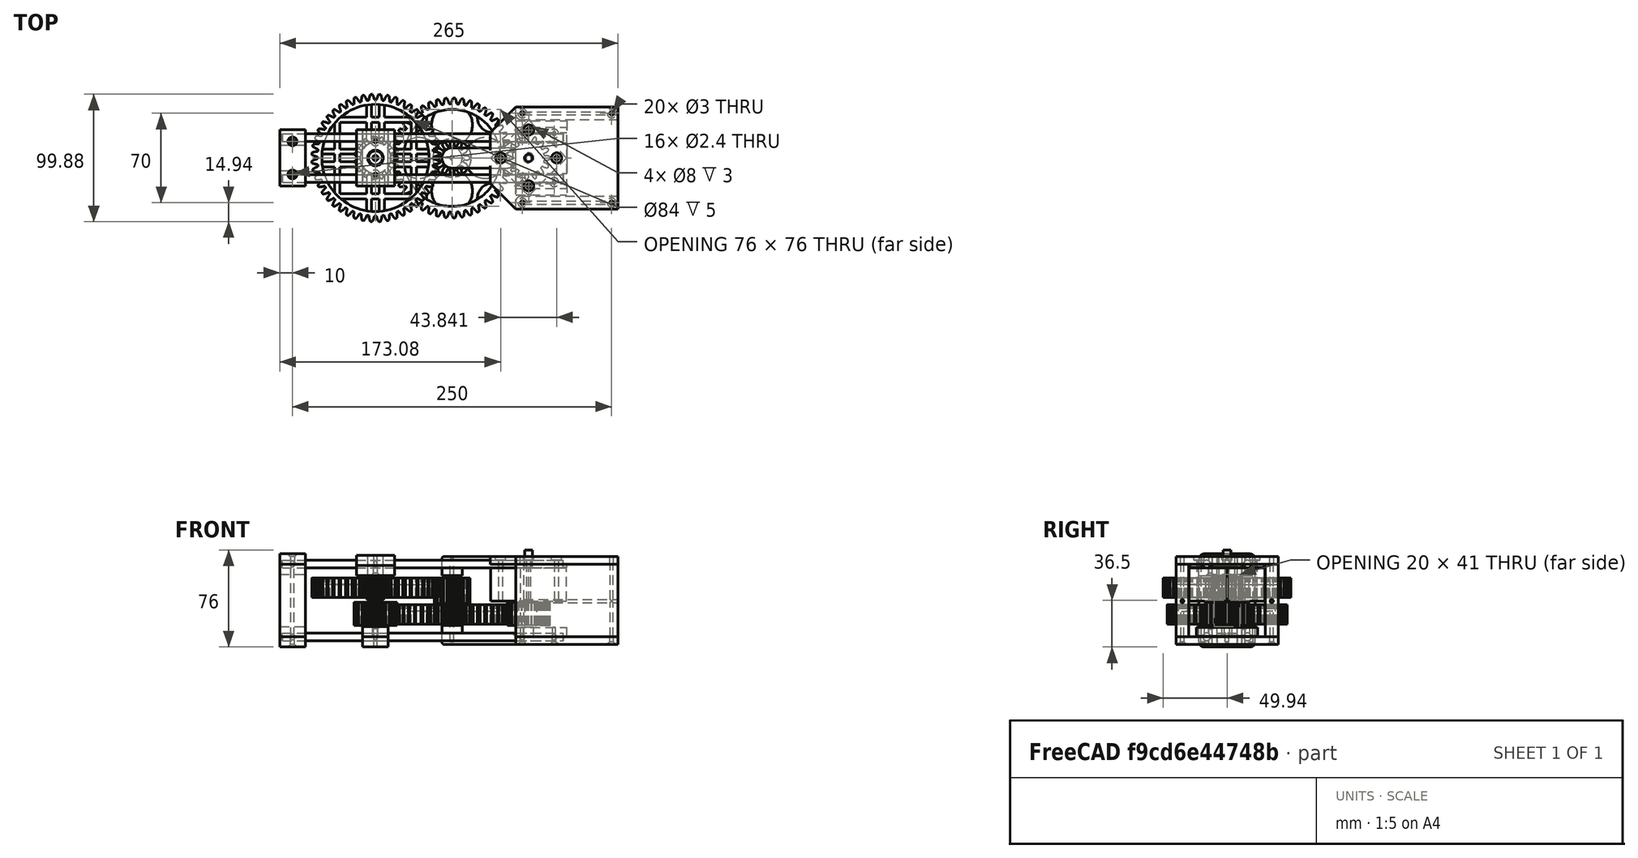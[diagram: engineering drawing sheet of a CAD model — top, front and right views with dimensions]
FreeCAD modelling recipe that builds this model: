
FCSTD DOCUMENT  (FreeCAD 0.18R16146 (Git))
Label: DoubleAxis2
License: All rights reserved
LicenseURL: http://en.wikipedia.org/wiki/All_rights_reserved
objects: Part::Cylinder×72, Part::MultiFuse×35, Part::Cut×28, Part::Box×21, Part::Feature×20, Part::Fillet×11, Part::Chamfer×6, Part::FeaturePython×5
note: 198 computed .brp shape members not serialized (recipe doc carries the construction recipe); baked Part::Feature solids carry a one-line shape summary decoded from their .brp

FEATURE [Part::Cylinder] Cylinder  label="CenterAxis"
  Angle = 360
  AttacherType = Attacher::AttachEngine3D
  Height = 100
  Placement = pos=(0,0,-10) rot=(0,0,1;0rad)
  Radius = 2.1
FEATURE [Part::FeaturePython] involutegear  label="MinuteGear"  # WARN: FeaturePython — macro-defined, semantics opaque (R4)
  Placement = pos=(0,0,1) rot=(0,0,1;0rad)
  backlash = 0
  beta = 0
  clearance = 0.25
  double_helix = false
  dw = 30
  head = 0
  height = 18
  module = 2
  numpoints = 6
  pressure_angle = 20
  properties_from_tool = false
  reversed_backlash = false
  shift = 0
  simple = false
  teeth = 15
  transverse_pitch = 6.28319
  undercut = false
  version = 0.0.3
FEATURE [Part::Cylinder] Cylinder004  label="Axis001"
  Angle = 360
  AttacherType = Attacher::AttachEngine3D
  Height = 50
  Radius = 2
FEATURE [Part::Cylinder] Cylinder005
  Angle = 360
  AttacherType = Attacher::AttachEngine3D
  Height = 19
  Placement = pos=(0,0,1) rot=(0,0,1;0rad)
  Radius = 6.5
FEATURE [Part::MultiFuse] Fusion
  Shapes = -> [Cylinder005,involutegear]
FEATURE [Part::Cut] Cut002  label="MinuteHandGear"
  Base = -> Fusion
  Placement = pos=(-60,0,0) rot=(0,0,1;0rad)
  Tool = -> Cylinder004
FEATURE [Part::Cylinder] Cylinder006  label="Bearing003"
  Angle = 360
  AttacherType = Attacher::AttachEngine3D
  Height = 15
  Placement = pos=(0,0,21) rot=(0,0,1;0rad)
  Radius = 5.5
FEATURE [Part::Cylinder] Cylinder007  label="Bearing002"
  Angle = 360
  AttacherType = Attacher::AttachEngine3D
  Height = 2
  Placement = pos=(0,0,21) rot=(0,0,1;0rad)
  Radius = 6.5
FEATURE [Part::MultiFuse] Fusion001  label="CenterBearingBody"
  Shapes = -> [Cylinder007,Cylinder006]
FEATURE [Part::Feature] Fusion001002004  label="Cutout005"
  Placement = pos=(0,0,0) rot=(0,0,-1;1.5708rad)
  shape: bbox 35 x 44.41 x 10 mm, 12 faces, 2 solids (baked)
FEATURE [Part::FeaturePython] involutegear002  label="HourGear"  # WARN: FeaturePython — macro-defined, semantics opaque (R4)
  Placement = pos=(0,0,0) rot=(0,0,1;0.064577rad)
  backlash = 0
  beta = 0
  clearance = 0.25
  double_helix = false
  dw = 96
  head = 0
  height = 15
  module = 2
  numpoints = 6
  pressure_angle = 20
  properties_from_tool = false
  reversed_backlash = false
  shift = 0
  simple = false
  teeth = 48
  transverse_pitch = 6.28319
  undercut = false
  version = 0.0.3
FEATURE [Part::Feature] Fusion001002003  label="Cutout004"
  Placement = pos=(0,0,0) rot=(0,0,1;3.14159rad)
  shape: bbox 44.41 x 35 x 10 mm, 12 faces, 2 solids (baked)
FEATURE [Part::Feature] Fusion001002002  label="Cutout003"
  Placement = pos=(0,0,0) rot=(0,0,1;1.5708rad)
  shape: bbox 35 x 44.41 x 10 mm, 12 faces, 2 solids (baked)
FEATURE [Part::Feature] Fusion001002001  label="Cutout002"
  shape: bbox 44.41 x 35 x 10 mm, 12 faces, 2 solids (baked)
FEATURE [Part::MultiFuse] Fusion001002005
  Shapes = -> [Fusion001002004,Fusion001002002,Fusion001002001,Fusion001002003]
FEATURE [Part::Cylinder] Cylinder008  label="Axis002"
  Angle = 360
  AttacherType = Attacher::AttachEngine3D
  Height = 16
  Radius = 12
FEATURE [Part::Cylinder] Cylinder009  label="Cutout001"
  Angle = 360
  AttacherType = Attacher::AttachEngine3D
  Height = 10
  Placement = pos=(0,0,10) rot=(0,0,1;0rad)
  Radius = 42
FEATURE [Part::Box] Box002  label="Cube002"
  AttacherType = Attacher::AttachEngine3D
  Height = 10
  Length = 64
  Placement = pos=(-32,-32,0) rot=(0,0,1;0rad)
  Width = 64
FEATURE [Part::Box] Box003  label="Cube003"
  AttacherType = Attacher::AttachEngine3D
  Height = 10
  Length = 56
  Placement = pos=(-28,-28,0) rot=(0,0,1;0rad)
  Width = 56
FEATURE [Part::Cut] Cut009
  Base = -> Box002
  Tool = -> Box003
FEATURE [Part::Cylinder] Cylinder012  label="Axis003"
  Angle = 360
  AttacherType = Attacher::AttachEngine3D
  Height = 50
  Radius = 6
FEATURE [Part::Cut] Cut
  Base = -> involutegear002
  Tool = -> Cylinder009
FEATURE [Part::MultiFuse] Fusion001002006
  Shapes = -> [Cut,Cylinder008]
FEATURE [Part::Cut] Cut010
  Base = -> Fusion001002006
  Tool = -> Fusion001002005
FEATURE [Part::MultiFuse] Fusion001002007
  Shapes = -> [Cut010,Cut009]
FEATURE [Part::Cut] Cut011  label="HourHandGear"
  Base = -> Fusion001002007
  Placement = pos=(-60,0,23) rot=(0,0,1;0rad)
  Tool = -> Cylinder012
FEATURE [Part::Cut] Cut012  label="CenterBearing001"
  Base = -> Fusion001
  Placement = pos=(-60,0,0) rot=(0,0,1;0rad)
  Tool = -> Cylinder
FEATURE [Part::FeaturePython] involutegear001  label="Couple001"  # WARN: FeaturePython — macro-defined, semantics opaque (R4)
  Placement = pos=(0,0,2) rot=(0,0,1;0rad)
  backlash = 0
  beta = 0
  clearance = 0.25
  double_helix = false
  dw = 90
  head = 0
  height = 15
  module = 2
  numpoints = 6
  pressure_angle = 20
  properties_from_tool = false
  reversed_backlash = false
  shift = 0
  simple = false
  teeth = 45
  transverse_pitch = 6.28319
  undercut = false
  version = 0.0.3
FEATURE [Part::FeaturePython] involutegear004  label="Couple003"  # WARN: FeaturePython — macro-defined, semantics opaque (R4)
  Placement = pos=(0,0,10) rot=(0,0,1;0rad)
  backlash = 0
  beta = 0
  clearance = 0.25
  double_helix = false
  dw = 24
  head = 0
  height = 28
  module = 2
  numpoints = 6
  pressure_angle = 20
  properties_from_tool = false
  reversed_backlash = false
  shift = 0
  simple = false
  teeth = 12
  transverse_pitch = 6.28319
  undercut = false
  version = 0.0.3
FEATURE [Part::FeaturePython] involutegear005  label="MotorGear002"  # WARN: FeaturePython — macro-defined, semantics opaque (R4)
  Placement = pos=(60,0,1) rot=(0,0,1;0rad)
  backlash = 0
  beta = 0
  clearance = 0.25
  double_helix = false
  dw = 30
  head = 0
  height = 18
  module = 2
  numpoints = 6
  pressure_angle = 20
  properties_from_tool = false
  reversed_backlash = false
  shift = 0
  simple = false
  teeth = 15
  transverse_pitch = 6.28319
  undercut = false
  version = 0.0.3
FEATURE [Part::Cylinder] Cylinder013  label="Cutout006"
  Angle = 360
  AttacherType = Attacher::AttachEngine3D
  Height = 5
  Placement = pos=(0,0,12) rot=(0,0,1;0rad)
  Radius = 38
FEATURE [Part::Cylinder] Cylinder014  label="Cylinder"
  Angle = 360
  AttacherType = Attacher::AttachEngine3D
  Height = 16
  Placement = pos=(0,0,2) rot=(0,0,1;0rad)
  Radius = 15
FEATURE [Part::Feature] Cut015001  label="Cut016"
  shape: bbox 28 x 48.41 x 16 mm, 8 faces, 2 solids (baked)
FEATURE [Part::Feature] Cut015002  label="Cut017"
  Placement = pos=(0,0,0) rot=(0,0,1;1.5708rad)
  shape: bbox 48.41 x 28 x 16 mm, 8 faces, 2 solids (baked)
FEATURE [Part::Feature] Cut015003  label="Cut018"
  Placement = pos=(0,0,0) rot=(0,0,1;3.14159rad)
  shape: bbox 28 x 48.41 x 16 mm, 8 faces, 2 solids (baked)
FEATURE [Part::Feature] Cut015004  label="Cut019"
  Placement = pos=(0,0,0) rot=(0,0,-1;1.5708rad)
  shape: bbox 48.41 x 28 x 16 mm, 8 faces, 2 solids (baked)
FEATURE [Part::MultiFuse] Fusion001002009
  Placement = pos=(0,0,-3) rot=(0,0,1;0rad)
  Shapes = -> [Cut015004,Cut015003,Cut015001,Cut015002]
FEATURE [Part::MultiFuse] Fusion001002010
  Shapes = -> [Cylinder013,Fusion001002009]
FEATURE [Part::Cut] Cut015005
  Base = -> involutegear001
  Tool = -> Fusion001002010
FEATURE [Part::Cylinder] Cylinder015  label="Cylinder006"
  Angle = 360
  AttacherType = Attacher::AttachEngine3D
  Height = 9
  Placement = pos=(0,0,30) rot=(0,0,1;0rad)
  Radius = 8
FEATURE [Part::MultiFuse] Fusion001002011
  Shapes = -> [Cylinder015,Cut015005,Cylinder014,involutegear004]
FEATURE [Part::Cylinder] Cylinder016  label="Axis004"
  Angle = 360
  AttacherType = Attacher::AttachEngine3D
  Height = 50
  Radius = 1.6
FEATURE [Part::Cut] Cut015006  label="CouplingGear001"
  Base = -> Fusion001002011
  Tool = -> Cylinder016
FEATURE [Part::Cylinder] Cylinder017  label="MotorAxis"
  Angle = 360
  AttacherType = Attacher::AttachEngine3D
  Height = 50
  Placement = pos=(60,0,0) rot=(0,0,1;0rad)
  Radius = 2
FEATURE [Part::Cut] Cut015007  label="MotorGear"
  Base = -> involutegear005
  Tool = -> Cylinder017
FEATURE [Part::Box] Box004  label="BottomBase001"
  AttacherType = Attacher::AttachEngine3D
  Height = 8
  Length = 20
  Placement = pos=(-135,-22,-16) rot=(0,0,1;0rad)
  Width = 44
FEATURE [Part::Cylinder] Cylinder020  label="ScrewHole"
  Angle = 360
  AttacherType = Attacher::AttachEngine3D
  Height = 40
  Placement = pos=(-125,13,-20) rot=(0,0,1;0rad)
  Radius = 1.5
FEATURE [Part::Cylinder] Cylinder021  label="ScrewHole001"
  Angle = 360
  AttacherType = Attacher::AttachEngine3D
  Height = 40
  Placement = pos=(-125,-13,-20) rot=(0,0,1;0rad)
  Radius = 1.5
FEATURE [Part::Box] Box005  label="BottomBase002"
  AttacherType = Attacher::AttachEngine3D
  Height = 57
  Length = 20
  Placement = pos=(-135,-22,-8) rot=(0,0,1;0rad)
  Width = 44
FEATURE [Part::Cylinder] Cylinder025  label="ScrewHole005"
  Angle = 360
  AttacherType = Attacher::AttachEngine3D
  Height = 100
  Placement = pos=(-125,-13,-20) rot=(0,0,1;0rad)
  Radius = 1.2
FEATURE [Part::Cylinder] Cylinder026  label="ScrewHole006"
  Angle = 360
  AttacherType = Attacher::AttachEngine3D
  Height = 100
  Placement = pos=(-125,13,-20) rot=(0,0,1;0rad)
  Radius = 1.2
FEATURE [Part::MultiFuse] Fusion001002012004
  Shapes = -> [Cylinder026,Cylinder025]
FEATURE [Part::Fillet] Fillet
  Base = -> Box004
  Edges = 2 edges r=4: [Edge9,Edge11]
FEATURE [Part::Box] Box008  label="BottomBase005"
  AttacherType = Attacher::AttachEngine3D
  Height = 41
  Length = 20
  Placement = pos=(-135,-10,0) rot=(0,0,1;0rad)
  Width = 20
FEATURE [Part::Fillet] Fillet002
  Base = -> Box008
  Edges = 4 edges r=9: [Edge9,Edge10,Edge11,Edge12]
FEATURE [Part::Box] Box009  label="MotorBody"
  AttacherType = Attacher::AttachEngine3D
  Height = 26
  Length = 42
  Placement = pos=(-21,-21,20) rot=(0,0,1;0rad)
  Width = 42
FEATURE [Part::Cylinder] Cylinder032  label="ScrewHole011"
  Angle = 360
  AttacherType = Attacher::AttachEngine3D
  Height = 50
  Placement = pos=(15.5,15.5,0) rot=(0,0,1;0rad)
  Radius = 1.6
FEATURE [Part::Cylinder] Cylinder033  label="ScrewHole002"
  Angle = 360
  AttacherType = Attacher::AttachEngine3D
  Height = 50
  Placement = pos=(-15.5,15.5,0) rot=(0,0,1;0rad)
  Radius = 1.6
FEATURE [Part::Cylinder] Cylinder034  label="ScrewHole012"
  Angle = 360
  AttacherType = Attacher::AttachEngine3D
  Height = 50
  Placement = pos=(15.5,-15.5,0) rot=(0,0,1;0rad)
  Radius = 1.6
FEATURE [Part::Cylinder] Cylinder035  label="ScrewHole013"
  Angle = 360
  AttacherType = Attacher::AttachEngine3D
  Height = 50
  Placement = pos=(-15.5,-15.5,0) rot=(0,0,1;0rad)
  Radius = 1.6
FEATURE [Part::MultiFuse] Fusion001002012013  label="MotorScrewHoles"
  Shapes = -> [Cylinder035,Cylinder033,Cylinder034,Cylinder032]
FEATURE [Part::Cut] Cut015008  label="MotorBody001"
  Base = -> Box009
  Tool = -> Fusion001002012013
FEATURE [Part::Cylinder] Cylinder036  label="MotorAxis001"
  Angle = 360
  AttacherType = Attacher::AttachEngine3D
  Height = 20
  Placement = pos=(0,0,40) rot=(0,0,1;0rad)
  Radius = 3
FEATURE [Part::MultiFuse] Fusion001002014  label="MotorModel"
  Placement = pos=(60,0,0) rot=(0,0,1;0.785398rad)
  Shapes = -> [Cut015008,Cylinder036]
FEATURE [Part::Cylinder] Cylinder037  label="HourAxis"
  Angle = 360
  AttacherType = Attacher::AttachEngine3D
  Height = 50
  Placement = pos=(-60,0,30) rot=(0,0,1;0rad)
  Radius = 6.1
FEATURE [Part::Box] Box019  label="BottomBase015"
  AttacherType = Attacher::AttachEngine3D
  Height = 8
  Length = 30
  Placement = pos=(-75,-22,40) rot=(0,0,1;0rad)
  Width = 44
FEATURE [Part::Cut] Cut015017007002
  Base = -> Box019
  Tool = -> Cylinder037
FEATURE [Part::Cylinder] Cylinder038  label="ScrewHole014"
  Angle = 360
  AttacherType = Attacher::AttachEngine3D
  Height = 100
  Placement = pos=(-60,-13,-20) rot=(0,0,1;0rad)
  Radius = 1.5
FEATURE [Part::Cylinder] Cylinder039  label="ScrewHole015"
  Angle = 360
  AttacherType = Attacher::AttachEngine3D
  Height = 100
  Placement = pos=(-60,13,-20) rot=(0,0,1;0rad)
  Radius = 1.5
FEATURE [Part::MultiFuse] Fusion001002012021
  Shapes = -> [Cylinder039,Cylinder038]
FEATURE [Part::Cut] Cut015017007003  label="HandCap001Body"
  Base = -> Cut015017007002
  Tool = -> Fusion001002012021
FEATURE [Part::Chamfer] Chamfer002  label="HandCap001"
  Base = -> Cut015017007003
  Edges = 2 edges r=2: [Edge16,Edge18]
FEATURE [Part::Box] Box  label="BoxBase"
  AttacherType = Attacher::AttachEngine3D
  Height = 6
  Length = 100
  Placement = pos=(30,-40,49) rot=(0,0,1;0rad)
  Width = 80
FEATURE [Part::Box] Box021  label="BoxBase001"
  AttacherType = Attacher::AttachEngine3D
  Height = 8.5
  Length = 90
  Placement = pos=(0,-8,46.5) rot=(0,0,1;0rad)
  Width = 16
FEATURE [Part::Cylinder] Cylinder043  label="Cylinder007"
  Angle = 360
  AttacherType = Attacher::AttachEngine3D
  Height = 15
  Placement = pos=(0,0,40) rot=(0,0,1;0rad)
  Radius = 8
FEATURE [Part::Fillet] Fillet010
  Base = -> Cylinder043
  Edges = 1 edges r=2: [Edge1]
FEATURE [Part::Cylinder] Cylinder047  label="Column003"
  Angle = 360
  AttacherType = Attacher::AttachEngine3D
  Height = 220
  Placement = pos=(-133,-16,-8) rot=(0,1,0;1.5708rad)
  Radius = 3
FEATURE [Part::Cylinder] Cylinder048  label="Column004"
  Angle = 360
  AttacherType = Attacher::AttachEngine3D
  Height = 220
  Placement = pos=(-133,16,-8) rot=(0,1,0;1.5708rad)
  Radius = 3
FEATURE [Part::MultiFuse] Fusion001002012029  label="BottomPilars"
  Shapes = -> [Cylinder047,Cylinder048]
FEATURE [Part::Cylinder] Cylinder049  label="Column005"
  Angle = 360
  AttacherType = Attacher::AttachEngine3D
  Height = 220
  Placement = pos=(-133,-16,49) rot=(0,1,0;1.5708rad)
  Radius = 3
FEATURE [Part::Cylinder] Cylinder050  label="Column006"
  Angle = 360
  AttacherType = Attacher::AttachEngine3D
  Height = 220
  Placement = pos=(-133,16,49) rot=(0,1,0;1.5708rad)
  Radius = 3
FEATURE [Part::MultiFuse] Fusion001002012030  label="TopPilars001"
  Shapes = -> [Cylinder049,Cylinder050]
FEATURE [Part::Feature] Fusion001002012029001  label="BottomPilars001"
  shape: bbox 220 x 38 x 6 mm, 6 faces, 2 solids (baked)
FEATURE [Part::MultiFuse] Fusion001002012029002
  Shapes = -> [Cylinder020,Cylinder021,Fusion001002012029001]
FEATURE [Part::Cut] Cut015017007008
  Base = -> Fillet
  Tool = -> Fusion001002012029002
FEATURE [Part::Chamfer] Chamfer  label="Cap001"
  Base = -> Cut015017007008
  Edges = 2 edges r=2: [Edge28,Edge29]
FEATURE [Part::Feature] Fusion001002012029003  label="BottomPilars002"
  shape: bbox 220 x 38 x 6 mm, 6 faces, 2 solids (baked)
FEATURE [Part::Feature] Fusion001002012030001  label="TopPilars002"
  shape: bbox 220 x 38 x 6 mm, 6 faces, 2 solids (baked)
FEATURE [Part::MultiFuse] Fusion001002012030002
  Shapes = -> [Fusion001002012004,Fillet002,Fusion001002012029003,Fusion001002012030001]
FEATURE [Part::Cut] Cut015017007009  label="CapJoin001"
  Base = -> Box005
  Tool = -> Fusion001002012030002
FEATURE [Part::Feature] Chamfer003  label="Cap002"
  Placement = pos=(0,0,41) rot=(1,0,0;3.14159rad)
  shape: bbox 20 x 44 x 8 mm, 16 faces (baked)
FEATURE [Part::Box] Box022  label="BottomBase017"
  AttacherType = Attacher::AttachEngine3D
  Height = 8
  Length = 20
  Placement = pos=(-70,-22,-8) rot=(0,0,1;0rad)
  Width = 44
FEATURE [Part::Cylinder] Cylinder051  label="ScrewHole018"
  Angle = 360
  AttacherType = Attacher::AttachEngine3D
  Height = 100
  Placement = pos=(-125,-13,-20) rot=(0,0,1;0rad)
  Radius = 1.5
FEATURE [Part::Cylinder] Cylinder052  label="ScrewHole019"
  Angle = 360
  AttacherType = Attacher::AttachEngine3D
  Height = 100
  Placement = pos=(-125,13,-20) rot=(0,0,1;0rad)
  Radius = 1.5
FEATURE [Part::MultiFuse] Fusion001002012030003
  Placement = pos=(65,0,0) rot=(0,0,1;0rad)
  Shapes = -> [Cylinder052,Cylinder051]
FEATURE [Part::Cylinder] Cylinder053  label="MinuteHandAxis"
  Angle = 360
  AttacherType = Attacher::AttachEngine3D
  Height = 60
  Placement = pos=(-60,0,-20) rot=(0,0,1;0rad)
  Radius = 2.1
FEATURE [Part::MultiFuse] Fusion001002012030004
  Shapes = -> [Fusion001002012030003,Cylinder053]
FEATURE [Part::Cut] Cut015017007010  label="Cap004Body"
  Base = -> Box022
  Tool = -> Fusion001002012030004
FEATURE [Part::Feature] Fusion001002012030005  label="TopPilars003"
  shape: bbox 220 x 38 x 6 mm, 6 faces, 2 solids (baked)
FEATURE [Part::Cut] Cut015017007011  label="Cap005"
  Base = -> Chamfer002
  Tool = -> Fusion001002012030005
FEATURE [Part::Box] Box023  label="BottomBase018"
  AttacherType = Attacher::AttachEngine3D
  Height = 8
  Length = 30
  Placement = pos=(-75,-22,48) rot=(0,0,1;0rad)
  Width = 44
FEATURE [Part::Cylinder] Cylinder054  label="ScrewHole020"
  Angle = 360
  AttacherType = Attacher::AttachEngine3D
  Height = 100
  Placement = pos=(-125,-13,-20) rot=(0,0,1;0rad)
  Radius = 1.2
FEATURE [Part::Cylinder] Cylinder055  label="ScrewHole021"
  Angle = 360
  AttacherType = Attacher::AttachEngine3D
  Height = 100
  Placement = pos=(-125,13,-20) rot=(0,0,1;0rad)
  Radius = 1.2
FEATURE [Part::MultiFuse] Fusion001002012030006
  Placement = pos=(65,0,0) rot=(0,0,1;0rad)
  Shapes = -> [Cylinder055,Cylinder054]
FEATURE [Part::Cylinder] Cylinder056  label="HourHandAxis001"
  Angle = 360
  AttacherType = Attacher::AttachEngine3D
  Height = 60
  Placement = pos=(-60,0,30) rot=(0,0,1;0rad)
  Radius = 6.1
FEATURE [Part::MultiFuse] Fusion001002012030007
  Shapes = -> [Fusion001002012030006,Cylinder056]
FEATURE [Part::Fillet] Fillet011
  Base = -> Box023
  Edges = 2 edges r=4: [Edge10,Edge12]
FEATURE [Part::Cut] Cut015017007012
  Base = -> Fillet011
  Tool = -> Fusion001002012030007
FEATURE [Part::Feature] Fusion001002012030008  label="TopPilars004"
  shape: bbox 220 x 38 x 6 mm, 6 faces, 2 solids (baked)
FEATURE [Part::Cut] Cut015017007013  label="Cap006"
  Base = -> Cut015017007012
  Tool = -> Fusion001002012030008
FEATURE [Part::Chamfer] Chamfer004  label="Cap004Body002"
  Base = -> Cut015017007010
  Edges = 2 edges r=2: [Edge10,Edge12]
FEATURE [Part::Box] Box024  label="BottomBase019"
  AttacherType = Attacher::AttachEngine3D
  Height = 8
  Length = 20
  Placement = pos=(-70,-22,-16) rot=(0,0,1;0rad)
  Width = 44
FEATURE [Part::Cylinder] Cylinder057  label="ScrewHole022"
  Angle = 360
  AttacherType = Attacher::AttachEngine3D
  Height = 100
  Placement = pos=(-125,-13,-20) rot=(0,0,1;0rad)
  Radius = 1.2
FEATURE [Part::Cylinder] Cylinder058  label="ScrewHole023"
  Angle = 360
  AttacherType = Attacher::AttachEngine3D
  Height = 100
  Placement = pos=(-125,13,-20) rot=(0,0,1;0rad)
  Radius = 1.2
FEATURE [Part::MultiFuse] Fusion001002012030009
  Placement = pos=(65,0,0) rot=(0,0,1;0rad)
  Shapes = -> [Cylinder058,Cylinder057]
FEATURE [Part::Fillet] Fillet012
  Base = -> Box024
  Edges = 2 edges r=4: [Edge9,Edge11]
FEATURE [Part::Feature] Fusion001002012029004  label="BottomPilars003"
  shape: bbox 220 x 38 x 6 mm, 6 faces, 2 solids (baked)
FEATURE [Part::Cut] Cut015017007014  label="Cap003Body"
  Base = -> Fillet012
  Tool = -> Fusion001002012029004
FEATURE [Part::Feature] Fusion001002012030010  label="BottomPilars004"
  shape: bbox 220 x 38 x 6 mm, 6 faces, 2 solids (baked)
FEATURE [Part::Cut] Cut015017007015  label="Cap004"
  Base = -> Chamfer004
  Tool = -> Fusion001002012030010
FEATURE [Part::Cut] Cut015017007016  label="Cap003"
  Base = -> Cut015017007014
  Tool = -> Fusion001002012030009
FEATURE [Part::Fillet] Fillet008
  Base = -> Box021
  Edges = 2 edges r=4: [Edge5,Edge7]
FEATURE [Part::Fillet] Fillet009
  Base = -> Fillet008
  Edges = 1 edges r=2: [Edge5]
FEATURE [Part::Box] Box025  label="BoxBase002"
  AttacherType = Attacher::AttachEngine3D
  Height = 8
  Length = 50
  Placement = pos=(40,-12,46.5) rot=(0,0,1;0rad)
  Width = 24
FEATURE [Part::Box] Box027  label="BoxBase004"
  AttacherType = Attacher::AttachEngine3D
  Height = 8
  Length = 40
  Placement = pos=(50,20,46.5) rot=(0,0,1;0rad)
  Width = 9
FEATURE [Part::Cylinder] Cylinder059  label="ScrewHole024"
  Angle = 360
  AttacherType = Attacher::AttachEngine3D
  Height = 50
  Placement = pos=(-15.5,15.5,0) rot=(0,0,1;0rad)
  Radius = 1.6
FEATURE [Part::Cylinder] Cylinder060  label="ScrewHole025"
  Angle = 360
  AttacherType = Attacher::AttachEngine3D
  Height = 50
  Placement = pos=(15.5,15.5,0) rot=(0,0,1;0rad)
  Radius = 1.6
FEATURE [Part::Cylinder] Cylinder061  label="ScrewHole026"
  Angle = 360
  AttacherType = Attacher::AttachEngine3D
  Height = 50
  Placement = pos=(15.5,-15.5,0) rot=(0,0,1;0rad)
  Radius = 1.6
FEATURE [Part::Cylinder] Cylinder062  label="ScrewHole027"
  Angle = 360
  AttacherType = Attacher::AttachEngine3D
  Height = 50
  Placement = pos=(-15.5,-15.5,0) rot=(0,0,1;0rad)
  Radius = 1.6
FEATURE [Part::MultiFuse] Fusion001002012030013  label="MotorScrewHoles001"
  Placement = pos=(60,0,20) rot=(0,0,1;0.785398rad)
  Shapes = -> [Cylinder062,Cylinder059,Cylinder061,Cylinder060]
FEATURE [Part::Cylinder] Cylinder063  label="ScrewHole028"
  Angle = 360
  AttacherType = Attacher::AttachEngine3D
  Height = 50
  Placement = pos=(15.5,-15.5,0) rot=(0,0,1;0rad)
  Radius = 4
FEATURE [Part::Cylinder] Cylinder064  label="ScrewHole029"
  Angle = 360
  AttacherType = Attacher::AttachEngine3D
  Height = 50
  Placement = pos=(15.5,15.5,0) rot=(0,0,1;0rad)
  Radius = 4
FEATURE [Part::Cylinder] Cylinder065  label="ScrewHole030"
  Angle = 360
  AttacherType = Attacher::AttachEngine3D
  Height = 50
  Placement = pos=(-15.5,15.5,0) rot=(0,0,1;0rad)
  Radius = 4
FEATURE [Part::Cylinder] Cylinder066  label="ScrewHole031"
  Angle = 360
  AttacherType = Attacher::AttachEngine3D
  Height = 50
  Placement = pos=(-15.5,-15.5,0) rot=(0,0,1;0rad)
  Radius = 4
FEATURE [Part::MultiFuse] Fusion001002012030014  label="MotorScrewHoles002"
  Placement = pos=(60,0,52) rot=(0,0,1;0.785398rad)
  Shapes = -> [Cylinder066,Cylinder065,Cylinder063,Cylinder064]
FEATURE [Part::Box] Box026  label="BoxBase003"
  AttacherType = Attacher::AttachEngine3D
  Height = 8
  Length = 40
  Placement = pos=(50,-29,46.5) rot=(0,0,1;0rad)
  Width = 9
FEATURE [Part::MultiFuse] Fusion001002012030011  label="BoxBase005"
  Shapes = -> [Fillet009,Box026,Box025,Box027,Box]
FEATURE [Part::MultiFuse] Fusion001002012030012  label="BoxBase006"
  Shapes = -> [Fusion001002012030011,Fillet010]
FEATURE [Part::Cylinder] Cylinder067  label="ScrewHole032"
  Angle = 360
  AttacherType = Attacher::AttachEngine3D
  Height = 50
  Placement = pos=(55,-35,0) rot=(0,0,1;0rad)
  Radius = 1.5
FEATURE [Part::Cylinder] Cylinder068  label="ScrewHole033"
  Angle = 360
  AttacherType = Attacher::AttachEngine3D
  Height = 50
  Placement = pos=(55,35,0) rot=(0,0,1;0rad)
  Radius = 1.5
FEATURE [Part::Cylinder] Cylinder069  label="ScrewHole034"
  Angle = 360
  AttacherType = Attacher::AttachEngine3D
  Height = 50
  Placement = pos=(125,35,0) rot=(0,0,1;0rad)
  Radius = 1.5
FEATURE [Part::Cylinder] Cylinder070  label="ScrewHole035"
  Angle = 360
  AttacherType = Attacher::AttachEngine3D
  Height = 50
  Placement = pos=(125,-35,0) rot=(0,0,1;0rad)
  Radius = 1.5
FEATURE [Part::MultiFuse] Fusion001002012030015  label="BoxScrewHoles"
  Placement = pos=(0,0,30) rot=(0,0,1;0rad)
  Shapes = -> [Cylinder070,Cylinder069,Cylinder067,Cylinder068]
FEATURE [Part::Cylinder] Cylinder071  label="ScrewHole036"
  Angle = 360
  AttacherType = Attacher::AttachEngine3D
  Height = 20
  Placement = pos=(0,0,33) rot=(0,0,1;0rad)
  Radius = 1.5
FEATURE [Part::MultiFuse] Fusion001002012030016  label="BoxHoles"
  Shapes = -> [Cylinder071,Fusion001002012030015,Fusion001002012030014,Fusion001002012030013]
FEATURE [Part::Feature] Fusion001002012030017  label="TopPilars005"
  shape: bbox 220 x 38 x 6 mm, 6 faces, 2 solids (baked)
FEATURE [Part::Box] Box030  label="BoxBase008"
  AttacherType = Attacher::AttachEngine3D
  Height = 8.5
  Length = 90
  Placement = pos=(0,-8,-14) rot=(0,0,1;0rad)
  Width = 16
FEATURE [Part::Cylinder] Cylinder077  label="Cylinder008"
  Angle = 360
  AttacherType = Attacher::AttachEngine3D
  Height = 15
  Placement = pos=(0,0,-14) rot=(0,0,1;0rad)
  Radius = 8
FEATURE [Part::Cylinder] Cylinder086  label="ScrewHole049"
  Angle = 360
  AttacherType = Attacher::AttachEngine3D
  Height = 50
  Placement = pos=(125,35,-20) rot=(0,0,1;0rad)
  Radius = 1.5
FEATURE [Part::Cylinder] Cylinder087  label="ScrewHole050"
  Angle = 360
  AttacherType = Attacher::AttachEngine3D
  Height = 50
  Placement = pos=(125,-35,-20) rot=(0,0,1;0rad)
  Radius = 1.5
FEATURE [Part::Cylinder] Cylinder088  label="ScrewHole051"
  Angle = 360
  AttacherType = Attacher::AttachEngine3D
  Height = 50
  Placement = pos=(55,35,-20) rot=(0,0,1;0rad)
  Radius = 1.5
FEATURE [Part::Cylinder] Cylinder089  label="ScrewHole052"
  Angle = 360
  AttacherType = Attacher::AttachEngine3D
  Height = 50
  Placement = pos=(55,-35,-20) rot=(0,0,1;0rad)
  Radius = 1.5
FEATURE [Part::Cylinder] Cylinder090  label="ScrewHole053"
  Angle = 360
  AttacherType = Attacher::AttachEngine3D
  Height = 20
  Placement = pos=(0,0,-12) rot=(0,0,1;0rad)
  Radius = 1.5
FEATURE [Part::Box] Box029  label="BoxBase007"
  AttacherType = Attacher::AttachEngine3D
  Height = 6
  Length = 80
  Placement = pos=(50,-40,-14) rot=(0,0,1;0rad)
  Width = 80
FEATURE [Part::Fillet] Fillet013
  Base = -> Box030
  Edges = 2 edges r=2: [Edge9,Edge11]
FEATURE [Part::Fillet] Fillet014
  Base = -> Cylinder077
  Edges = 1 edges r=2: [Edge3]
FEATURE [Part::MultiFuse] Fusion001002012030027
  Shapes = -> [Fillet013,Fillet014,Box029]
FEATURE [Part::Feature] Fusion001002012029005  label="BottomPilars005"
  shape: bbox 220 x 38 x 6 mm, 6 faces, 2 solids (baked)
FEATURE [Part::Box] Box031  label="Cube"
  AttacherType = Attacher::AttachEngine3D
  Height = 10
  Length = 60
  Placement = pos=(47,-10,-8) rot=(0,0,1;0rad)
  Width = 20
FEATURE [Part::Box] Box032  label="BottomBase020"
  AttacherType = Attacher::AttachEngine3D
  Height = 7
  Length = 40
  Placement = pos=(50,-24,-7.5) rot=(0,0,1;0rad)
  Width = 48
FEATURE [Part::Feature] Fusion001002012030030  label="BottomPilars006"
  shape: bbox 220 x 38 x 6 mm, 6 faces, 2 solids (baked)
FEATURE [Part::Cut] Cut015017007025
  Base = -> Box032
  Tool = -> Fusion001002012030030
FEATURE [Part::Cylinder] Cylinder097  label="Cylinder015"
  Angle = 360
  AttacherType = Attacher::AttachEngine3D
  Height = 30
  Placement = pos=(55,19,-20) rot=(0,0,1;0rad)
  Radius = 1.5
FEATURE [Part::Cylinder] Cylinder098  label="Cylinder016"
  Angle = 360
  AttacherType = Attacher::AttachEngine3D
  Height = 30
  Placement = pos=(80,19,-20) rot=(0,0,1;0rad)
  Radius = 1.5
FEATURE [Part::Cylinder] Cylinder099  label="Cylinder017"
  Angle = 360
  AttacherType = Attacher::AttachEngine3D
  Height = 30
  Placement = pos=(80,-19,-20) rot=(0,0,1;0rad)
  Radius = 1.5
FEATURE [Part::Cylinder] Cylinder100  label="Cylinder018"
  Angle = 360
  AttacherType = Attacher::AttachEngine3D
  Height = 30
  Placement = pos=(55,-19,-20) rot=(0,0,1;0rad)
  Radius = 1.5
FEATURE [Part::Cylinder] Cylinder101  label="Cylinder019"
  Angle = 360
  AttacherType = Attacher::AttachEngine3D
  Height = 30
  Placement = pos=(55,19,-20) rot=(0,0,1;0rad)
  Radius = 1.2
FEATURE [Part::Cylinder] Cylinder102  label="Cylinder020"
  Angle = 360
  AttacherType = Attacher::AttachEngine3D
  Height = 30
  Placement = pos=(80,19,-20) rot=(0,0,1;0rad)
  Radius = 1.2
FEATURE [Part::Cylinder] Cylinder103  label="Cylinder021"
  Angle = 360
  AttacherType = Attacher::AttachEngine3D
  Height = 30
  Placement = pos=(80,-19,-20) rot=(0,0,1;0rad)
  Radius = 1.2
FEATURE [Part::Cylinder] Cylinder104  label="Cylinder022"
  Angle = 360
  AttacherType = Attacher::AttachEngine3D
  Height = 30
  Placement = pos=(55,-19,-20) rot=(0,0,1;0rad)
  Radius = 1.2
FEATURE [Part::MultiFuse] Fusion001002012030033  label="ScrewHoles001"
  Shapes = -> [Cylinder104,Cylinder101,Cylinder102,Cylinder103]
FEATURE [Part::Cylinder] Cylinder105  label="Cylinder023"
  Angle = 360
  AttacherType = Attacher::AttachEngine3D
  Height = 10
  Placement = pos=(60,0,-10) rot=(0,0,1;0rad)
  Radius = 4
FEATURE [Part::MultiFuse] Fusion001002012030034
  Shapes = -> [Cylinder105,Fusion001002012030033]
FEATURE [Part::Cut] Cut015017007028  label="PillarHolder001"
  Base = -> Cut015017007025
  Tool = -> Fusion001002012030034
FEATURE [Part::Chamfer] Chamfer006
  Base = -> Box031
  Edges = 1 edges r=3: [Edge4]
FEATURE [Part::Cut] Cut015017007029  label="BoxBotomBody"
  Base = -> Fusion001002012030027
  Tool = -> Chamfer006
FEATURE [Part::MultiFuse] Fusion001002012030035  label="ScrewHoles"
  Shapes = -> [Cylinder089,Cylinder100,Cylinder097,Cylinder088,Cylinder098,Cylinder099,Cylinder087,Cylinder086,Cylinder090]
FEATURE [Part::MultiFuse] Fusion001002012030036  label="BotomHolows"
  Shapes = -> [Fusion001002012030035,Fusion001002012029005]
FEATURE [Part::Cut] Cut015017007030
  Base = -> Cut015017007029
  Tool = -> Fusion001002012030036
FEATURE [Part::Chamfer] Chamfer007  label="BotomBoxCover"
  Base = -> Cut015017007030
  Edges = 8 edges r=2: [Edge58,Edge59,Edge60,Edge61,Edge62,Edge63,Edge64,Edge65]
FEATURE [Part::Feature] Fusion001002014001  label="MotorModel001"
  shape: bbox 59.4 x 59.4 x 40 mm, 12 faces (baked)
FEATURE [Part::Box] Box037  label="BottomBase025"
  AttacherType = Attacher::AttachEngine3D
  Height = 57
  Length = 80
  Placement = pos=(50,30,-8) rot=(0,0,1;0rad)
  Width = 10
FEATURE [Part::Box] Box038  label="BottomBase026"
  AttacherType = Attacher::AttachEngine3D
  Height = 57
  Length = 80
  Placement = pos=(50,-40,-8) rot=(0,0,1;0rad)
  Width = 10
FEATURE [Part::Fillet] Fillet015
  Base = -> Box038
  Edges = 1 edges r=4: [Edge3]
FEATURE [Part::Fillet] Fillet016
  Base = -> Box037
  Edges = 1 edges r=4: [Edge1]
FEATURE [Part::Cylinder] Cylinder106  label="ScrewHole054"
  Angle = 360
  AttacherType = Attacher::AttachEngine3D
  Height = 100
  Placement = pos=(125,35,-20) rot=(0,0,1;0rad)
  Radius = 1.2
FEATURE [Part::Cylinder] Cylinder107  label="ScrewHole055"
  Angle = 360
  AttacherType = Attacher::AttachEngine3D
  Height = 100
  Placement = pos=(125,-35,-20) rot=(0,0,1;0rad)
  Radius = 1.2
FEATURE [Part::Cylinder] Cylinder108  label="ScrewHole056"
  Angle = 360
  AttacherType = Attacher::AttachEngine3D
  Height = 100
  Placement = pos=(55,-35,-20) rot=(0,0,1;0rad)
  Radius = 1.2
FEATURE [Part::Cylinder] Cylinder109  label="ScrewHole057"
  Angle = 360
  AttacherType = Attacher::AttachEngine3D
  Height = 100
  Placement = pos=(55,35,-20) rot=(0,0,1;0rad)
  Radius = 1.2
FEATURE [Part::Cylinder] Cylinder110  label="ScrewHole058"
  Angle = 360
  AttacherType = Attacher::AttachEngine3D
  Height = 100
  Placement = pos=(55,-35,20) rot=(0,1,0;1.5708rad)
  Radius = 1.2
FEATURE [Part::Cylinder] Cylinder111  label="ScrewHole059"
  Angle = 360
  AttacherType = Attacher::AttachEngine3D
  Height = 100
  Placement = pos=(55,35,20) rot=(0,1,0;1.5708rad)
  Radius = 1.2
FEATURE [Part::MultiFuse] Fusion001002012030037
  Shapes = -> [Cylinder108,Cylinder107,Cylinder110]
FEATURE [Part::MultiFuse] Fusion001002012030038
  Shapes = -> [Cylinder106,Cylinder109,Cylinder111]
FEATURE [Part::Cut] Cut015017007031  label="Side001"
  Base = -> Fillet015
  Tool = -> Fusion001002012030037
FEATURE [Part::Cut] Cut015017007032  label="Side002"
  Base = -> Fillet016
  Tool = -> Fusion001002012030038
FEATURE [Part::MultiFuse] Fusion001002012030039
  Shapes = -> [Fusion001002014,Fusion001002012030016,Fusion001002012030017]
FEATURE [Part::Chamfer] Chamfer008
  Base = -> Fusion001002012030012
  Edges = 2 edges r=20: [Edge34,Edge58]
FEATURE [Part::Cut] Cut015017007033  label="TopBoxCover"
  Base = -> Chamfer008
  Tool = -> Fusion001002012030039
